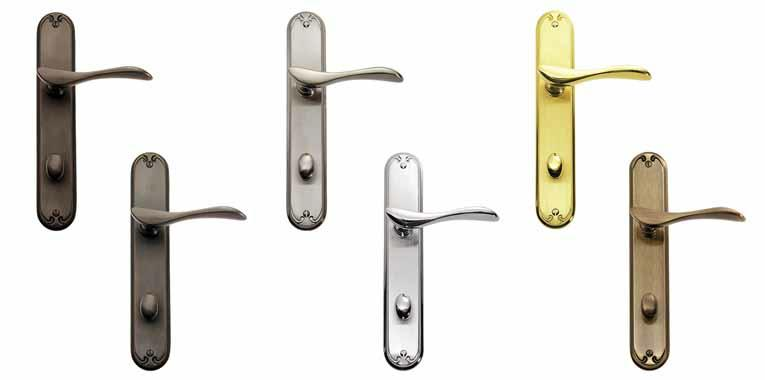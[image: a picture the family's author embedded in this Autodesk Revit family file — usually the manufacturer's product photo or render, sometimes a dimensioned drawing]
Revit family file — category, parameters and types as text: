
# Revit family: Door-French-Pella-Architect_Series-Hinged_Patio_Door-OutSwing-Right_Left
name_source: partatom
category: Doors
revit_build: Autodesk Revit Architecture 2013 (Build: 20130531_2115(x64)
units: mm (PartAtom-declared; Revit-internal decimal feet)

## types (30) — shared parameters
Analytic Construction = <None>
Architectural Design Manual = www.pellaadm.com
Construction Type = -
Cross Grille Pattern = No
Custom Grille Pattern = No
Custom Horizontal Lites = 2
Custom Vertical Lites = 6
Description = Out-Swing - Right Left Hand Operation
Door Grille Visibility = Yes
Door Handle Height = 3' - 0"
Energy Efficiency = http://www.pella.com
Environmental Commitment = http://www.pella.com
Ext Finish = Aluminum - Pella - Brown
Function = Interior
Glazing Finish = Glass - Pella - Clear Insulating Glass
Glazing Thickness = 107/128"
Int Finish = Wood - Pella - Pine
Manufacturer = Pella - Windows & Doors
Note* = Maximum Frame Depth is 211 mm; if Wall Depth exceeds this value please recalculated Set Back to reflect
Operation = Hinged Patio Door
Prairie Grille Pattern = No
Product Documentation Link = http://media.pella.com
Product Name = Architect Series Hinged Patio Door
Product Page URL = http://www.pella.com
Series = Architect Series - Aluminum-Clad Wood
Top Row Grille Pattern = No
Traditional Grille Pattern = Yes
URL = www.pella.com
Wall Closure = By host

## per-type parameters (varying)
| type | C Height | C Width | DLO Height | DLO Width | Height | Hinges | Rough Height | Rough Width | Unit Height | Unit Width | Width |
| 2680 | 6' - 7 1/2" | 2' - 1 3/8" | 5' - 4 127/256" | 1' - 1 3/16" | 6' - 7 1/2" | 3 | 6' - 8" | 2' - 2 1/8" | 6' - 5 3/8" | 1' - 11 31/256" | 2' - 1 3/8" |
| 2681 | 6' - 8 1/8" | 2' - 1 3/8" | 5' - 5 31/256" | 1' - 1 3/16" | 6' - 8 1/8" | 3 | 6' - 8 5/8" | 2' - 2 1/8" | 6' - 6" | 1' - 11 31/256" | 2' - 1 3/8" |
| 2682 | 6' - 9 1/2" | 2' - 1 3/8" | 5' - 6 127/256" | 1' - 1 3/16" | 6' - 9 1/2" | 3 | 6' - 10" | 2' - 2 1/8" | 6' - 7 3/8" | 1' - 11 31/256" | 2' - 1 3/8" |
| 2686 | 7' - 2" | 2' - 1 3/8" | 5' - 10 255/256" | 1' - 1 3/16" | 7' - 2" | 4 | 7' - 2 1/2" | 2' - 2 1/8" | 6' - 11 7/8" | 1' - 11 31/256" | 2' - 1 3/8" |
| 2696 | 7' - 11 1/2" | 2' - 1 3/8" | 6' - 8 127/256" | 1' - 1 3/16" | 7' - 11 1/2" | 4 | 8' - 0" | 2' - 2 1/8" | 7' - 9 3/8" | 1' - 11 31/256" | 2' - 1 3/8" |
| 26120 | 9' - 11 1/2" | 2' - 1 3/8" | 8' - 8 127/256" | 1' - 1 3/16" | 9' - 11 1/2" | 4 | 10' - 0" | 2' - 2 1/8" | 9' - 9 3/8" | 1' - 11 31/256" | 2' - 1 3/8" |
| 3080 | 6' - 7 1/2" | 2' - 6" | 5' - 4 127/256" | 1' - 5 13/16" | 6' - 7 1/2" | 3 | 6' - 8" | 2' - 6 3/4" | 6' - 5 3/8" | 2' - 3 191/256" | 2' - 6" |
| 3081 | 6' - 8 1/8" | 2' - 6" | 5' - 5 31/256" | 1' - 5 13/16" | 6' - 8 1/8" | 3 | 6' - 8 5/8" | 2' - 6 3/4" | 6' - 6" | 2' - 3 191/256" | 2' - 6" |
| 3082 | 6' - 9 1/2" | 2' - 6" | 5' - 6 127/256" | 1' - 5 13/16" | 6' - 9 1/2" | 3 | 6' - 10" | 2' - 6 3/4" | 6' - 7 3/8" | 2' - 3 191/256" | 2' - 6" |
| 3086 | 7' - 2" | 2' - 6" | 5' - 10 255/256" | 1' - 5 13/16" | 7' - 2" | 4 | 7' - 2 1/2" | 2' - 6 3/4" | 6' - 11 7/8" | 2' - 3 191/256" | 2' - 6" |
| 3096 | 7' - 11 1/2" | 2' - 6" | 6' - 8 127/256" | 1' - 5 13/16" | 7' - 11 1/2" | 4 | 8' - 0" | 2' - 6 3/4" | 7' - 9 3/8" | 2' - 3 191/256" | 2' - 6" |
| 30120 | 9' - 11 1/2" | 2' - 6" | 8' - 8 127/256" | 1' - 5 13/16" | 9' - 11 1/2" | 4 | 10' - 0" | 2' - 6 3/4" | 9' - 9 3/8" | 2' - 3 191/256" | 2' - 6" |
| 3480 | 6' - 7 1/2" | 2' - 9 1/2" | 5' - 4 127/256" | 1' - 9 5/16" | 6' - 7 1/2" | 3 | 6' - 8" | 2' - 10 1/4" | 6' - 5 3/8" | 2' - 7 63/256" | 2' - 9 1/2" |
| 3481 | 6' - 8 1/8" | 2' - 9 1/2" | 5' - 5 31/256" | 1' - 9 5/16" | 6' - 8 1/8" | 3 | 6' - 8 5/8" | 2' - 10 1/4" | 6' - 6" | 2' - 7 63/256" | 2' - 9 1/2" |
| 3482 | 6' - 9 1/2" | 2' - 9 1/2" | 5' - 6 127/256" | 1' - 9 5/16" | 6' - 9 1/2" | 3 | 6' - 10" | 2' - 10 1/4" | 6' - 7 3/8" | 2' - 7 63/256" | 2' - 9 1/2" |
| 3486 | 7' - 2" | 2' - 9 1/2" | 5' - 10 255/256" | 1' - 9 5/16" | 7' - 2" | 4 | 7' - 2 1/2" | 2' - 10 1/4" | 6' - 11 7/8" | 2' - 7 63/256" | 2' - 9 1/2" |
| 3496 | 7' - 11 1/2" | 2' - 9 1/2" | 6' - 8 127/256" | 1' - 9 5/16" | 7' - 11 1/2" | 4 | 8' - 0" | 2' - 10 1/4" | 7' - 9 3/8" | 2' - 7 63/256" | 2' - 9 1/2" |
| 34120 | 9' - 11 1/2" | 2' - 9 1/2" | 8' - 8 127/256" | 1' - 9 5/16" | 9' - 11 1/2" | 4 | 10' - 0" | 2' - 10 1/4" | 9' - 9 3/8" | 2' - 7 63/256" | 2' - 9 1/2" |
| 3680 | 6' - 7 1/2" | 3' - 0" | 5' - 4 127/256" | 1' - 11 13/16" | 6' - 7 1/2" | 3 | 6' - 8" | 3' - 0 3/4" | 6' - 5 3/8" | 2' - 9 191/256" | 3' - 0" |
| 3681 | 6' - 8 1/8" | 3' - 0" | 5' - 5 31/256" | 1' - 11 13/16" | 6' - 8 1/8" | 3 | 6' - 8 5/8" | 3' - 0 3/4" | 6' - 6" | 2' - 9 191/256" | 3' - 0" |
| 3682 | 6' - 9 1/2" | 3' - 0" | 5' - 6 127/256" | 1' - 11 13/16" | 6' - 9 1/2" | 3 | 6' - 10" | 3' - 0 3/4" | 6' - 7 3/8" | 2' - 9 191/256" | 3' - 0" |
| 3686 | 7' - 2" | 3' - 0" | 5' - 10 255/256" | 1' - 11 13/16" | 7' - 2" | 4 | 7' - 2 1/2" | 3' - 0 3/4" | 6' - 11 7/8" | 2' - 9 191/256" | 3' - 0" |
| 3696 | 7' - 11 1/2" | 3' - 0" | 6' - 8 127/256" | 1' - 11 13/16" | 7' - 11 1/2" | 4 | 8' - 0" | 3' - 0 3/4" | 7' - 9 3/8" | 2' - 9 191/256" | 3' - 0" |
| 36120 | 9' - 11 1/2" | 3' - 0" | 8' - 8 127/256" | 1' - 11 13/16" | 9' - 11 1/2" | 4 | 10' - 0" | 3' - 0 3/4" | 9' - 9 3/8" | 2' - 9 191/256" | 3' - 0" |
| 3880 | 6' - 7 1/2" | 3' - 1 7/8" | 5' - 4 127/256" | 2' - 1 11/16" | 6' - 7 1/2" | 3 | 6' - 8" | 3' - 2 5/8" | 6' - 5 3/8" | 2' - 11 159/256" | 3' - 1 7/8" |
| 3881 | 6' - 8 1/8" | 3' - 1 7/8" | 5' - 5 31/256" | 2' - 1 11/16" | 6' - 8 1/8" | 3 | 6' - 8 5/8" | 3' - 2 5/8" | 6' - 6" | 2' - 11 159/256" | 3' - 1 7/8" |
| 3882 | 6' - 9 1/2" | 3' - 1 7/8" | 5' - 6 127/256" | 2' - 1 11/16" | 6' - 9 1/2" | 3 | 6' - 10" | 3' - 2 5/8" | 6' - 7 3/8" | 2' - 11 159/256" | 3' - 1 7/8" |
| 3886 | 7' - 2" | 3' - 1 7/8" | 5' - 10 255/256" | 2' - 1 11/16" | 7' - 2" | 4 | 7' - 2 1/2" | 3' - 2 5/8" | 6' - 11 7/8" | 2' - 11 159/256" | 3' - 1 7/8" |
| 3896 | 7' - 11 1/2" | 3' - 1 7/8" | 6' - 8 127/256" | 2' - 1 11/16" | 7' - 11 1/2" | 4 | 8' - 0" | 3' - 2 5/8" | 7' - 9 3/8" | 2' - 11 159/256" | 3' - 1 7/8" |
| 38120 | 9' - 11 1/2" | 3' - 1 7/8" | 8' - 8 127/256" | 2' - 1 11/16" | 9' - 11 1/2" | 4 | 10' - 0" | 3' - 2 5/8" | 9' - 9 3/8" | 2' - 11 159/256" | 3' - 1 7/8" |

note: column(s) folded — value = type name in every type: Model

## geometry (parser evidence)
native form markers: Blend x6, Sweep x11
no freeform markers — native parametric forms only
